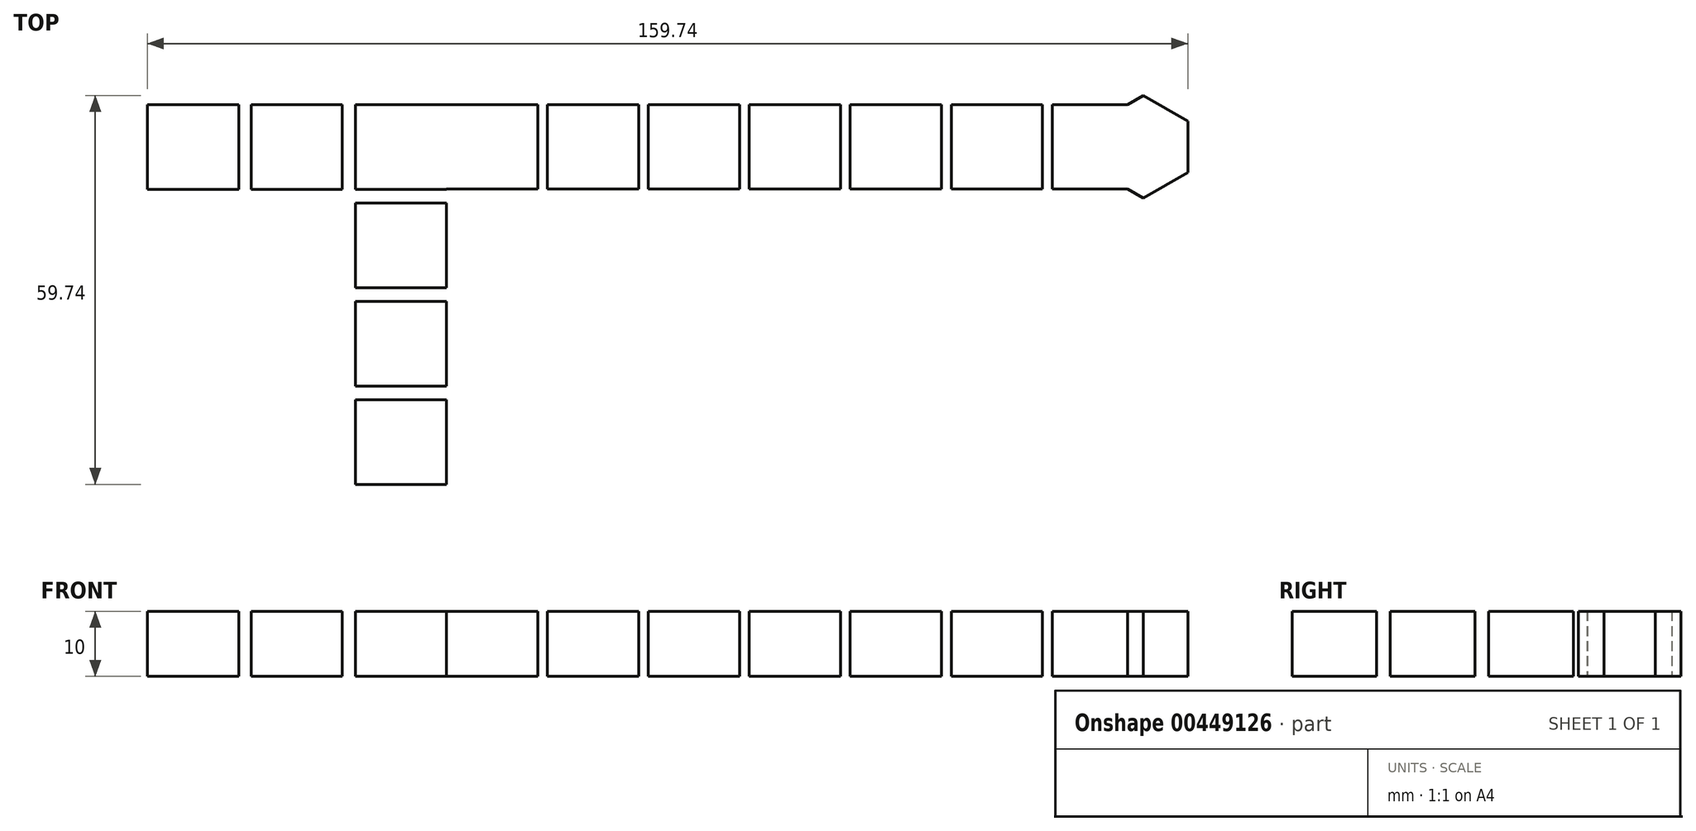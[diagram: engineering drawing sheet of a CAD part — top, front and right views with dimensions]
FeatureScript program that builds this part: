
annotation { "Feature Type Name" : "Feature", "Feature Type Description" : "" }
export const myFeature = defineFeature(function(context is Context, id is Id, definition is map)
    precondition{}
    {
        {
            var Q0;
            Q0=qCreatedBy(makeId("Top.planeOp"),FACE);
            var sketch = newSketch(context, id + "F0", { "sketchPlane" : qUnion([Q0])});
            skLineSegment(sketch, "E0.bottom", {"start": v(0, 0) * mm, "end": v(14, 0) * mm});
            skLineSegment(sketch, "E0.top", {"start": v(0, 13) * mm, "end": v(14, 13) * mm});
            skLineSegment(sketch, "E0.left", {"start": v(0, 0) * mm, "end": v(0, 13) * mm});
            skLineSegment(sketch, "E0.right", {"start": v(14, 0) * mm, "end": v(14, 13) * mm});
            skLineSegment(sketch, "E1.1.0.0", {"start": v(15.5, 13) * mm, "end": v(29.5, 13) * mm});
            skLineSegment(sketch, "E1.1.0.1", {"start": v(15.5, 0) * mm, "end": v(15.5, 13) * mm});
            skLineSegment(sketch, "E1.1.0.2", {"start": v(15.5, 0) * mm, "end": v(29.5, 0) * mm});
            skLineSegment(sketch, "E1.1.0.3", {"start": v(29.5, 0) * mm, "end": v(29.5, 13) * mm});
            skLineSegment(sketch, "E1.2.0.0", {"start": v(31, 13) * mm, "end": v(45, 13) * mm});
            skLineSegment(sketch, "E1.2.0.1", {"start": v(31, 0) * mm, "end": v(31, 13) * mm});
            skLineSegment(sketch, "E1.2.0.2", {"start": v(31, 0) * mm, "end": v(45, 0) * mm});
            skLineSegment(sketch, "E1.2.0.3", {"start": v(45, 0) * mm, "end": v(45, 13) * mm});
            skLineSegment(sketch, "E1.3.0.0", {"start": v(46.5, 13) * mm, "end": v(60.5, 13) * mm});
            skLineSegment(sketch, "E1.3.0.1", {"start": v(46.5, 0) * mm, "end": v(46.5, 13) * mm});
            skLineSegment(sketch, "E1.3.0.2", {"start": v(46.5, 0) * mm, "end": v(60.5, 0) * mm});
            skLineSegment(sketch, "E1.3.0.3", {"start": v(60.5, 0) * mm, "end": v(60.5, 13) * mm});
            skLineSegment(sketch, "E1.4.0.0", {"start": v(62, 13) * mm, "end": v(76, 13) * mm});
            skLineSegment(sketch, "E1.4.0.1", {"start": v(62, 0) * mm, "end": v(62, 13) * mm});
            skLineSegment(sketch, "E1.4.0.2", {"start": v(62, 0) * mm, "end": v(76, 0) * mm});
            skLineSegment(sketch, "E1.4.0.3", {"start": v(76, 0) * mm, "end": v(76, 13) * mm});
            skLineSegment(sketch, "E1.5.0.0", {"start": v(77.5, 13) * mm, "end": v(91.5, 13) * mm});
            skLineSegment(sketch, "E1.5.0.1", {"start": v(77.5, 0) * mm, "end": v(77.5, 13) * mm});
            skLineSegment(sketch, "E1.5.0.2", {"start": v(77.5, 0) * mm, "end": v(91.5, 0) * mm});
            skLineSegment(sketch, "E1.5.0.3", {"start": v(91.5, 0) * mm, "end": v(91.5, 13) * mm});
            skLineSegment(sketch, "E1.6.0.0", {"start": v(93, 13) * mm, "end": v(107, 13) * mm});
            skLineSegment(sketch, "E1.6.0.1", {"start": v(93, 0) * mm, "end": v(93, 13) * mm});
            skLineSegment(sketch, "E1.6.0.2", {"start": v(93, 0) * mm, "end": v(107, 0) * mm});
            skLineSegment(sketch, "E1.direction1", {"start": v(0, 13) * mm, "end": v(15.5, 13) * mm, "construction": true});
            skLineSegment(sketch, "E2.bottom", {"start": v(0, -32.35) * mm, "end": v(-14, -32.35) * mm});
            skLineSegment(sketch, "E2.top", {"start": v(0, -45.35) * mm, "end": v(-14, -45.35) * mm});
            skLineSegment(sketch, "E2.left", {"start": v(0, -32.35) * mm, "end": v(0, -45.35) * mm});
            skLineSegment(sketch, "E2.right", {"start": v(-14, -32.35) * mm, "end": v(-14, -45.35) * mm});
            skLineSegment(sketch, "E3.0.1.0", {"start": v(0, -17.25) * mm, "end": v(-14, -17.25) * mm});
            skLineSegment(sketch, "E3.0.1.1", {"start": v(-14, -17.25) * mm, "end": v(-14, -30.25) * mm});
            skLineSegment(sketch, "E3.0.1.2", {"start": v(0, -30.25) * mm, "end": v(-14, -30.25) * mm});
            skLineSegment(sketch, "E3.0.1.3", {"start": v(0, -17.25) * mm, "end": v(0, -30.25) * mm});
            skLineSegment(sketch, "E3.0.2.0", {"start": v(0, -2.15) * mm, "end": v(-14, -2.15) * mm});
            skLineSegment(sketch, "E3.0.2.1", {"start": v(-14, -2.15) * mm, "end": v(-14, -15.15) * mm});
            skLineSegment(sketch, "E3.0.2.2", {"start": v(0, -15.15) * mm, "end": v(-14, -15.15) * mm});
            skLineSegment(sketch, "E3.0.2.3", {"start": v(0, -2.15) * mm, "end": v(0, -15.15) * mm});
            skLineSegment(sketch, "E3.0.3.0", {"start": v(0, 12.95) * mm, "end": v(-14, 12.95) * mm});
            skLineSegment(sketch, "E3.0.3.1", {"start": v(-14, 12.95) * mm, "end": v(-14, -0.05) * mm});
            skLineSegment(sketch, "E3.0.3.2", {"start": v(0, -0.05) * mm, "end": v(-14, -0.05) * mm});
            skLineSegment(sketch, "E3.0.3.3", {"start": v(0, 12.95) * mm, "end": v(0, -0.05) * mm});
            skLineSegment(sketch, "E3.direction1", {"start": v(-14, -32.35) * mm, "end": v(11, -32.35) * mm, "construction": true});
            skLineSegment(sketch, "E3.direction2", {"start": v(-14, -32.35) * mm, "end": v(-14, -17.25) * mm, "construction": true});
            skCircle(sketch, "E4.cCircle", {"center": v(107, 6.5) * mm, "radius": 6.83 * mm, "construction": true});
            skLineSegment(sketch, "E4.0", {"start": v(113.83, 10.44) * mm, "end": v(113.83, 2.56) * mm});
            skLineSegment(sketch, "E4.1", {"start": v(113.83, 2.56) * mm, "end": v(107, -1.39) * mm});
            skLineSegment(sketch, "E4.2", {"start": v(107, -1.39) * mm, "end": v(100.17, 2.56) * mm});
            skLineSegment(sketch, "E4.3", {"start": v(100.17, 2.56) * mm, "end": v(100.17, 10.44) * mm});
            skLineSegment(sketch, "E4.4", {"start": v(100.17, 10.44) * mm, "end": v(107, 14.39) * mm});
            skLineSegment(sketch, "E4.5", {"start": v(107, 14.39) * mm, "end": v(113.83, 10.44) * mm});
            skPoint(sketch, "E4.0.midPoint", {"position": v(113.83, 6.5) * mm});
            skLineSegment(sketch, "E5.bottom", {"start": v(-45.9, -0.05) * mm, "end": v(-31.9, -0.05) * mm});
            skLineSegment(sketch, "E5.top", {"start": v(-45.9, 12.95) * mm, "end": v(-31.9, 12.95) * mm});
            skLineSegment(sketch, "E5.left", {"start": v(-45.9, -0.05) * mm, "end": v(-45.9, 12.95) * mm});
            skLineSegment(sketch, "E5.right", {"start": v(-31.9, -0.05) * mm, "end": v(-31.9, 12.95) * mm});
            skLineSegment(sketch, "E6.1.0.0", {"start": v(-30, 12.95) * mm, "end": v(-16, 12.95) * mm});
            skLineSegment(sketch, "E6.1.0.1", {"start": v(-16, -0.05) * mm, "end": v(-16, 12.95) * mm});
            skLineSegment(sketch, "E6.1.0.2", {"start": v(-30, -0.05) * mm, "end": v(-16, -0.05) * mm});
            skLineSegment(sketch, "E6.1.0.3", {"start": v(-30, -0.05) * mm, "end": v(-30, 12.95) * mm});
            skLineSegment(sketch, "E6.direction1", {"start": v(-45.9, 12.95) * mm, "end": v(-30, 12.95) * mm, "construction": true});
            skArc(sketch, "E7", {"start": v(0, -15.15) * mm, "mid": v(10.31, -10.64) * mm, "end": v(14, 0) * mm});
            skLineSegment(sketch, "E8.bottom", {"start": v(-31.9, 6.45) * mm, "end": v(-30, 6.45) * mm});
            skLineSegment(sketch, "E8.top", {"start": v(-31.9, 6.45) * mm, "end": v(-30, 6.45) * mm});
            skLineSegment(sketch, "E8.left", {"start": v(-31.9, 6.45) * mm, "end": v(-31.9, 6.45) * mm});
            skLineSegment(sketch, "E8.right", {"start": v(-30, 6.45) * mm, "end": v(-30, 6.45) * mm});
            skLineSegment(sketch, "E9.bottom", {"start": v(-16, 6.45) * mm, "end": v(-14, 6.45) * mm});
            skLineSegment(sketch, "E9.top", {"start": v(-16, 6.45) * mm, "end": v(-14, 6.45) * mm});
            skLineSegment(sketch, "E9.left", {"start": v(-16, 6.45) * mm, "end": v(-16, 6.45) * mm});
            skLineSegment(sketch, "E9.right", {"start": v(-14, 6.45) * mm, "end": v(-14, 6.45) * mm});
            skLineSegment(sketch, "E10.bottom", {"start": v(14, 6.5) * mm, "end": v(15.5, 6.5) * mm});
            skLineSegment(sketch, "E10.top", {"start": v(14, 6.5) * mm, "end": v(15.5, 6.5) * mm});
            skLineSegment(sketch, "E10.left", {"start": v(14, 6.5) * mm, "end": v(14, 6.5) * mm});
            skLineSegment(sketch, "E10.right", {"start": v(15.5, 6.5) * mm, "end": v(15.5, 6.5) * mm});
            skLineSegment(sketch, "E11.bottom", {"start": v(29.5, 6.5) * mm, "end": v(31, 6.5) * mm});
            skLineSegment(sketch, "E11.top", {"start": v(29.5, 6.5) * mm, "end": v(31, 6.5) * mm});
            skLineSegment(sketch, "E11.left", {"start": v(29.5, 6.5) * mm, "end": v(29.5, 6.5) * mm});
            skLineSegment(sketch, "E11.right", {"start": v(31, 6.5) * mm, "end": v(31, 6.5) * mm});
            skLineSegment(sketch, "E12.bottom", {"start": v(45, 6.5) * mm, "end": v(46.5, 6.5) * mm});
            skLineSegment(sketch, "E12.top", {"start": v(45, 6.5) * mm, "end": v(46.5, 6.5) * mm});
            skLineSegment(sketch, "E12.left", {"start": v(45, 6.5) * mm, "end": v(45, 6.5) * mm});
            skLineSegment(sketch, "E12.right", {"start": v(46.5, 6.5) * mm, "end": v(46.5, 6.5) * mm});
            skLineSegment(sketch, "E13.bottom", {"start": v(60.5, 6.5) * mm, "end": v(62, 6.5) * mm});
            skLineSegment(sketch, "E13.top", {"start": v(60.5, 6.5) * mm, "end": v(62, 6.5) * mm});
            skLineSegment(sketch, "E13.left", {"start": v(60.5, 6.5) * mm, "end": v(60.5, 6.5) * mm});
            skLineSegment(sketch, "E13.right", {"start": v(62, 6.5) * mm, "end": v(62, 6.5) * mm});
            skLineSegment(sketch, "E14.bottom", {"start": v(76, 6.5) * mm, "end": v(77.5, 6.5) * mm});
            skLineSegment(sketch, "E14.top", {"start": v(76, 6.5) * mm, "end": v(77.5, 6.5) * mm});
            skLineSegment(sketch, "E14.left", {"start": v(76, 6.5) * mm, "end": v(76, 6.5) * mm});
            skLineSegment(sketch, "E14.right", {"start": v(77.5, 6.5) * mm, "end": v(77.5, 6.5) * mm});
            skLineSegment(sketch, "E15.bottom", {"start": v(91.5, 6.5) * mm, "end": v(93, 6.5) * mm});
            skLineSegment(sketch, "E15.top", {"start": v(91.5, 6.5) * mm, "end": v(93, 6.5) * mm});
            skLineSegment(sketch, "E15.left", {"start": v(91.5, 6.5) * mm, "end": v(91.5, 6.5) * mm});
            skLineSegment(sketch, "E15.right", {"start": v(93, 6.5) * mm, "end": v(93, 6.5) * mm});
            skLineSegment(sketch, "E16.bottom", {"start": v(-7, -15.15) * mm, "end": v(-7, -15.15) * mm});
            skLineSegment(sketch, "E16.top", {"start": v(-7, -17.25) * mm, "end": v(-7, -17.25) * mm});
            skLineSegment(sketch, "E16.left", {"start": v(-7, -15.15) * mm, "end": v(-7, -17.25) * mm});
            skLineSegment(sketch, "E16.right", {"start": v(-7, -15.15) * mm, "end": v(-7, -17.25) * mm});
            skLineSegment(sketch, "E17.bottom", {"start": v(-7, -30.25) * mm, "end": v(-7, -30.25) * mm});
            skLineSegment(sketch, "E17.top", {"start": v(-7, -32.35) * mm, "end": v(-7, -32.35) * mm});
            skLineSegment(sketch, "E17.left", {"start": v(-7, -30.25) * mm, "end": v(-7, -32.35) * mm});
            skLineSegment(sketch, "E17.right", {"start": v(-7, -30.25) * mm, "end": v(-7, -32.35) * mm});
            skSolve(sketch);
        }
        {
            var Q0;
            Q0 = qSketchRegion(id + "F0", true);
            extrude(context, id + "F1", {"entities" : qUnion([Q0]), "depth" : 10 * mm});
        }
    });
